# Revit family: Edelstahlrohrschelle V4A, ohne AG, ohne VS, Ø321-360
name_source: partatom
category: HLS-Bauteile
units: mm (PartAtom-declared; Revit-internal decimal feet)

## family parameters
Arbeitsebenenbasiert = Ja
Beim Laden mit Abzugskörper schneiden = Nein
Bemaßung runder Anschluss = Durchmesser verwenden
Beschriftungsausrichtung beibehalten = Nein
Gemeinsam genutzt = Ja
Immer vertikal = Nein
Raumberechnungspunkt = Nein
Teiletyp = Normal

## types (2) — shared parameters
A = 5 mm  [stored 0.0164042 ft]
AB = 4 mm  [stored 0.0131234 ft]
Anschluss = ohne Anschluss
Bauart = zweiteilig
Breite Material = 50 mm
DF1 = 32 mm  [stored 0.104987 ft]
DF2 = 37 mm  [stored 0.121391 ft]
DVS = 17 mm
Fabrikat = MEFA
Firma = MEFA Befestigungs- und Montagesysteme GmbH
Kurztext1 = Rohrschelle Edelstahl V4A 50x5 mm
MB = 50 mm  [stored 0.164042 ft]
MD = 5 mm  [stored 0.0164042 ft]
Material = Edelstahl
Materialmaße = 50x5,0 mm
Materialname = V4A
Mengeneinheit = St
Schalldämmeinlage = ohne Dämmung
Stärke Material = 5 mm  [stored 0.0164042 ft]
Verschluss = Schraubenverschluss
Vorgabe-Ansicht = 1219 mm
max. zul. Last horizontal = 0.00 kN
max. zul. Last vertikal = 0.00 kN
vpe = 1
zero-valued in all types: HGA, Nennweite DN Rohr, Rohraußendurchmesser

## per-type parameters (varying)
| type | Achsabstand | Artikelnummer | B | Breite | D | Dmax | Dmin | EAN | Gewicht | Gewicht pro Bauteil | H | Kurztext2 | R | RM | Rohraußendurchmesser Zoll | S | max. Höhe | max. Rohraußendurchmesser | min. Höhe | min. Rohraußendurchmesser |
| Edelstahlrohrschelle V4A, o.AG, o.VS, Ø321-325 | 372 mm | 0495046 | 404 mm  [stored 1.32546 ft] | 404 mm  [stored 1.32546 ft] | 325 mm  [stored 1.06627 ft] | 325 mm  [stored 1.06627 ft] | 321 mm  [stored 1.05315 ft] | 4250928413413 | 2.27 kg | 2.27 kg | 335 mm  [stored 1.09908 ft] | 321 - 325 mm ohne Anschluss o. Dämm. | 163 mm | 168 mm | 12 Zoll | 372 mm  [stored 1.22047 ft] | 335 mm  [stored 1.09908 ft] | 325 mm  [stored 1.06627 ft] | 331 mm  [stored 1.08596 ft] | 321 mm  [stored 1.05315 ft] |
| Edelstahlrohrschelle V4A, o.AG, o.VS, Ø356-360 | 407 mm | 0495051 | 439 mm  [stored 1.44029 ft] | 439 mm  [stored 1.44029 ft] | 360 mm  [stored 1.1811 ft] | 360 mm  [stored 1.1811 ft] | 356 mm  [stored 1.16798 ft] | 4250928413420 | 2.50 kg | 2.50 kg | 370 mm  [stored 1.21391 ft] | 356 - 360 mm ohne Anschluss o. Dämm. | 180 mm  [stored 0.590551 ft] | 185 mm  [stored 0.606955 ft] | 14 Zoll | 407 mm  [stored 1.3353 ft] | 370 mm  [stored 1.21391 ft] | 360 mm  [stored 1.1811 ft] | 336 mm  [stored 1.10236 ft] | 356 mm  [stored 1.16798 ft] |

note: [stored X ft] marks values corroborated as IEEE doubles in the binary element streams (Revit-internal decimal feet)
